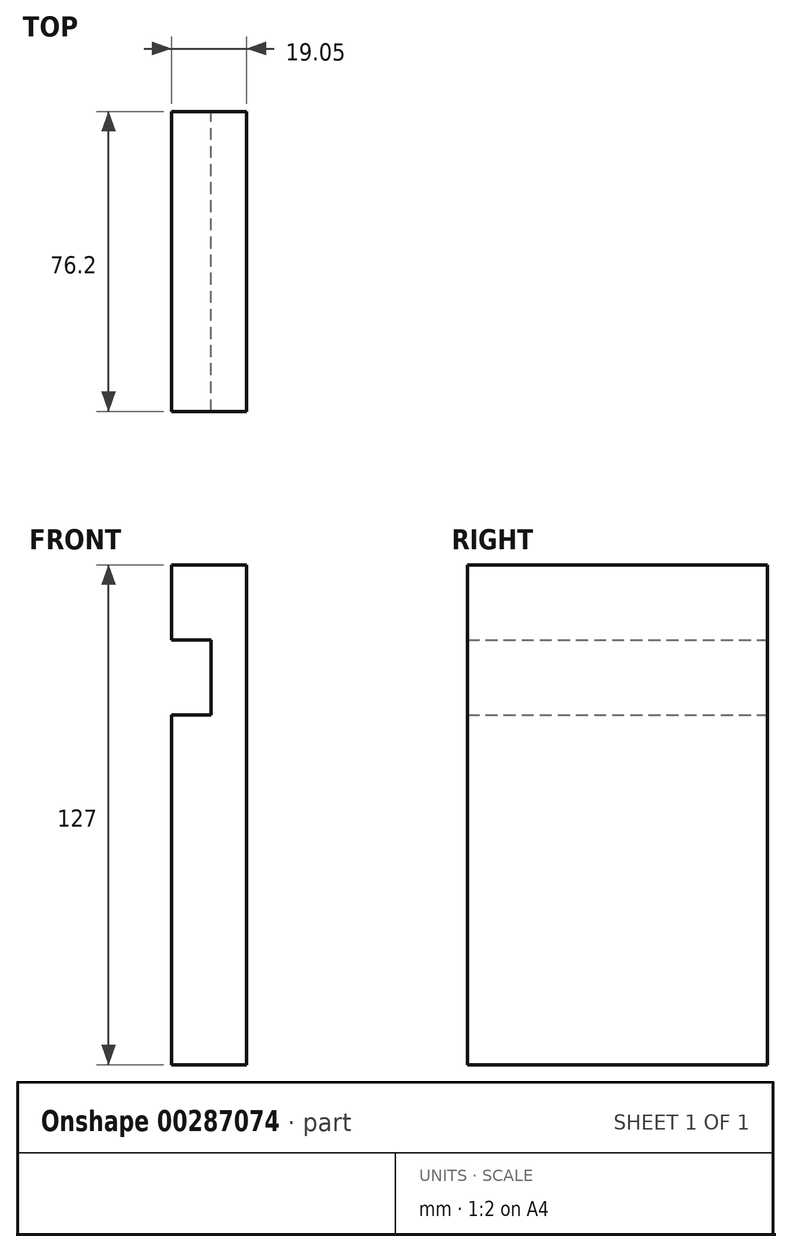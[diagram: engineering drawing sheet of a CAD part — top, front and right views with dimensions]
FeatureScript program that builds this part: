
annotation { "Feature Type Name" : "Feature", "Feature Type Description" : "" }
export const myFeature = defineFeature(function(context is Context, id is Id, definition is map)
    precondition{}
    {
        {
            var Q0;
            Q0=qCreatedBy(makeId("Front.planeOp"),FACE);
            var sketch = newSketch(context, id + "F0", { "sketchPlane" : qUnion([Q0])});
            skLineSegment(sketch, "E0", {"start": v(0, 0) * mm, "end": v(0, 127) * mm});
            skLineSegment(sketch, "E1", {"start": v(0, 127) * mm, "end": v(-19.05, 127) * mm});
            skLineSegment(sketch, "E2", {"start": v(-19.05, 127) * mm, "end": v(-19.05, 107.95) * mm});
            skLineSegment(sketch, "E3", {"start": v(-19.05, 107.95) * mm, "end": v(-9.02, 107.95) * mm});
            skLineSegment(sketch, "E4", {"start": v(-9.02, 107.95) * mm, "end": v(-9.02, 88.9) * mm});
            skLineSegment(sketch, "E5", {"start": v(-9.02, 88.9) * mm, "end": v(-19.05, 88.9) * mm});
            skLineSegment(sketch, "E6", {"start": v(-19.05, 88.9) * mm, "end": v(-19.05, 0) * mm});
            skLineSegment(sketch, "E7", {"start": v(-19.05, 0) * mm, "end": v(0, 0) * mm});
            skSolve(sketch);
        }
        {
            var Q0;
            Q0 = qSketchRegion(id + "F0", true);
            extrude(context, id + "F1", {"entities" : qUnion([Q0]), "depth" : 76.2 * mm});
        }
    });
